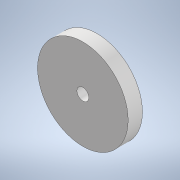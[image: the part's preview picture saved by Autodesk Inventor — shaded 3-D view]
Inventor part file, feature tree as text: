
AUTODESK INVENTOR PART (.ipt)
format: ipt  version: 2021 (Build 250183000, 183)  size: 99,328 bytes
history: native  units: mm
features: extrude x2, sketch x2
ambient origin geometry x8: Origin, YZ Plane, XZ Plane, XY Plane, X Axis, Y Axis, Z Axis, Center Point
bodies: Solid1 (feature_tree)
feature tree (4):
  extrude  "Extrusion1"  Depth=6.0mm TaperAngle=0.0deg
  extrude  "Extrusion2"  Depth=6.0mm TaperAngle=0.0deg
  sketch  "Sketch1"  dims[d0=38.0mm d1=6.0mm d2=0.0mm]
  sketch  "Sketch2"  dims[d3=5.0mm d4=6.0mm d5=0.0mm]
